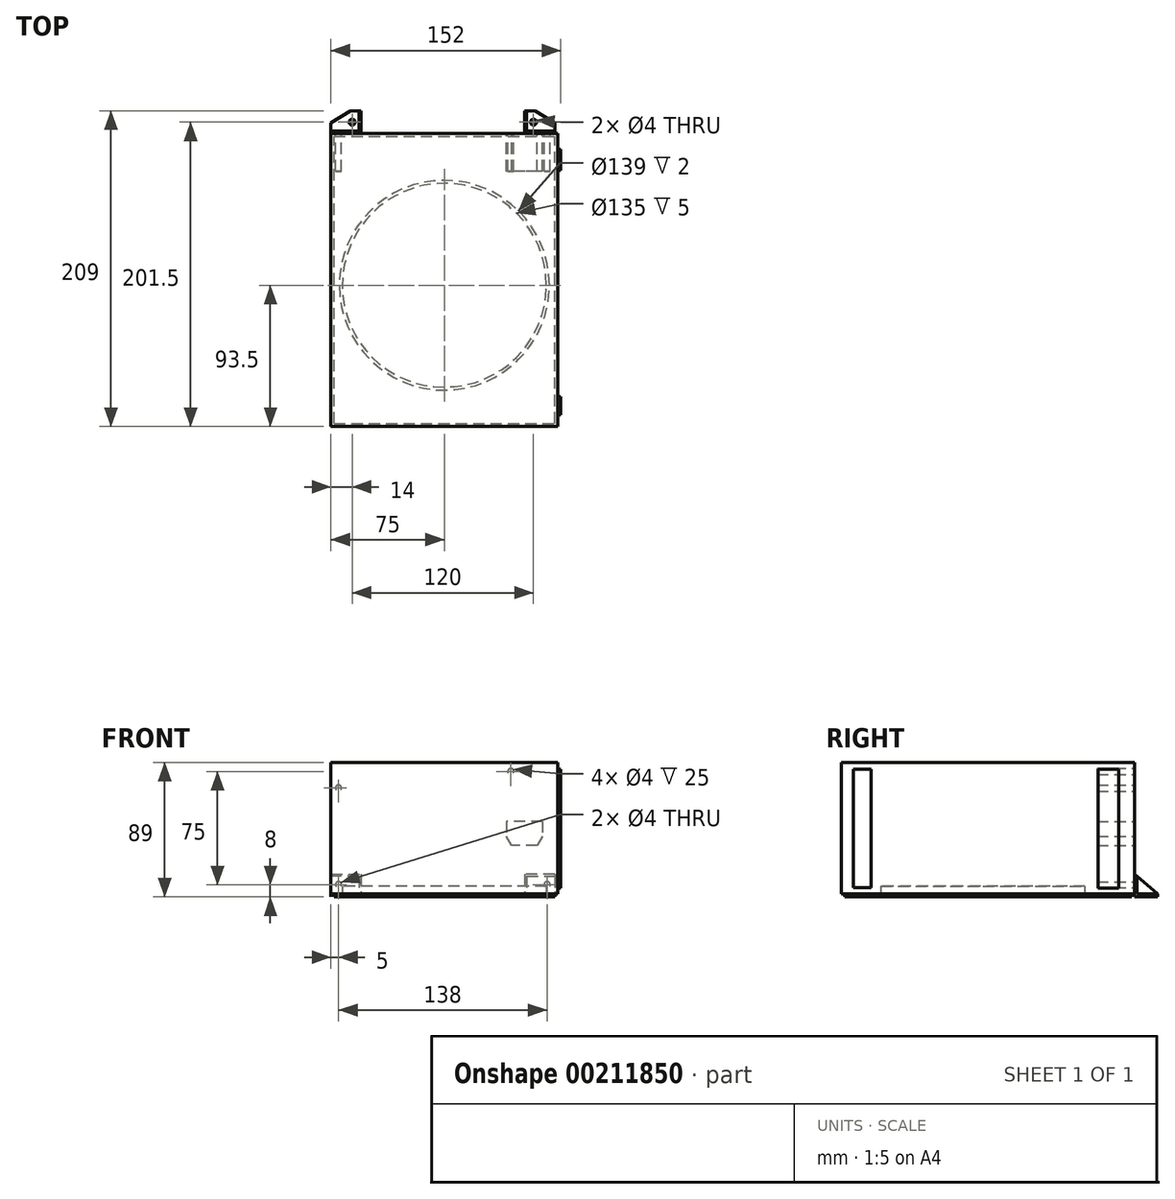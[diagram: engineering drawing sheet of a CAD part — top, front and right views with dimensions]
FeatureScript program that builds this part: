
annotation { "Feature Type Name" : "Feature", "Feature Type Description" : "" }
export const myFeature = defineFeature(function(context is Context, id is Id, definition is map)
    precondition{}
    {
        {
            var Q0;
            Q0=qCreatedBy(makeId("Top.planeOp"),FACE);
            var sketch = newSketch(context, id + "F0", { "sketchPlane" : qUnion([Q0])});
            skLineSegment(sketch, "E0.bottom", {"start": v(-75, 97) * mm, "end": v(75, 97) * mm});
            skLineSegment(sketch, "E0.top", {"start": v(-75, -97) * mm, "end": v(75, -97) * mm});
            skLineSegment(sketch, "E0.left", {"start": v(-75, 97) * mm, "end": v(-75, -97) * mm});
            skLineSegment(sketch, "E0.right", {"start": v(75, 97) * mm, "end": v(75, -97) * mm});
            skLineSegment(sketch, "E1", {"start": v(0, 0) * mm, "end": v(0, 97) * mm, "construction": true});
            skLineSegment(sketch, "E2", {"start": v(0, 0) * mm, "end": v(0, -97) * mm, "construction": true});
            skLineSegment(sketch, "E3", {"start": v(0, 0) * mm, "end": v(75, 0) * mm, "construction": true});
            skLineSegment(sketch, "E4", {"start": v(0, 0) * mm, "end": v(-75, 0) * mm, "construction": true});
            skCircle(sketch, "E5", {"center": v(0, -3.5) * mm, "radius": 67.5 * mm});
            skSolve(sketch);
        }
        {
            var Q0;
            Q0=makeQuery(id+"F0.imprint","IMPRINT",FACE,{"disambiguationData":[TD([[makeQuery(id+"F0.imprint","IMPRINT",EDGE,{"derivedFrom":sQuery(id+"F0.wireOp",EDGE,"E0.bottom")}),-1.0]])]});
            var Q1;
            Q1=makeQuery(id+"F0.imprint","IMPRINT",FACE,{"disambiguationData":[TD([[makeQuery(id+"F0.imprint","IMPRINT",EDGE,{"derivedFrom":sQuery(id+"F0.wireOp",EDGE,"E5")}),1.0]])]});
            extrude(context, id + "F1", {"entities" : qUnion([Q0, Q1]), "depth" : 87 * mm});
        }
        {
            var Q0;
            Q0=makeQuery(id+"F0.imprint","IMPRINT",FACE,{"disambiguationData":[TD([[makeQuery(id+"F0.imprint","IMPRINT",EDGE,{"derivedFrom":sQuery(id+"F0.wireOp",EDGE,"E5")}),1.0]])]});
            extrude(context, id + "F2", {"entities" : qUnion([Q0]), "operationType" : NewBodyOperationType.REMOVE, "depth" : 5 * mm});
        }
        {
            var Q0;
            Q0=makeQuery(id+"F1.opExtrude","SWEPT_FACE",FACE,{"disambiguationData":[OSD([sQuery(id+"F0.wireOp",EDGE,"E0.bottom")])]});
            var sketch = newSketch(context, id + "F3", { "sketchPlane" : qUnion([Q0])});
            skLineSegment(sketch, "E6.bottom", {"start": v(-65, 48) * mm, "end": v(-41, 48) * mm});
            skLineSegment(sketch, "E6.top", {"start": v(-61.5, 32) * mm, "end": v(-44.5, 32) * mm});
            skLineSegment(sketch, "E6.left", {"start": v(-65, 48) * mm, "end": v(-65, 38.06) * mm});
            skLineSegment(sketch, "E6.right", {"start": v(-41, 48) * mm, "end": v(-41, 38.06) * mm});
            skLineSegment(sketch, "E7", {"start": v(-65, 38.06) * mm, "end": v(-61.5, 32) * mm});
            skLineSegment(sketch, "E8", {"start": v(-44.5, 32) * mm, "end": v(-41, 38.06) * mm});
            skPoint(sketch, "E9.orphan", {"position": v(-65, 32) * mm});
            skPoint(sketch, "E10.orphan", {"position": v(-41, 32) * mm});
            skCircle(sketch, "E11", {"center": v(-44, 81) * mm, "radius": 2 * mm});
            skCircle(sketch, "E12", {"center": v(70, 70) * mm, "radius": 2 * mm});
            skCircle(sketch, "E13", {"center": v(70, 6) * mm, "radius": 2 * mm});
            skCircle(sketch, "E14", {"center": v(-68, 6) * mm, "radius": 2 * mm});
            skLineSegment(sketch, "E15", {"start": v(-91.51, 6) * mm, "end": v(111.2, 6) * mm, "construction": true});
            skLineSegment(sketch, "E16", {"start": v(70, 99.51) * mm, "end": v(70, -34.47) * mm, "construction": true});
            skSolve(sketch);
        }
        {
            var Q0;
            Q0 = qSketchRegion(id + "F3", true);
            extrude(context, id + "F4", {"entities" : qUnion([Q0]), "operationType" : NewBodyOperationType.REMOVE, "oppositeDirection" : true, "depth" : 25 * mm});
        }
        {
            var Q0;
            Q0=makeQuery(id+"F1.opExtrude","CAP_FACE",FACE,{"disambiguationData":[OSD([sQuery(id+"F0.wireOp",EDGE,"E0.bottom"),sQuery(id+"F0.wireOp",EDGE,"E0.top"),sQuery(id+"F0.wireOp",EDGE,"E0.left"),sQuery(id+"F0.wireOp",EDGE,"E0.right")])],"isStart":true});
            var sketch = newSketch(context, id + "F5", { "sketchPlane" : qUnion([Q0])});
            skLineSegment(sketch, "E17.bottom", {"start": v(-73, 95) * mm, "end": v(73, 95) * mm});
            skLineSegment(sketch, "E17.top", {"start": v(-73, -95) * mm, "end": v(73, -95) * mm});
            skLineSegment(sketch, "E17.left", {"start": v(-73, 95) * mm, "end": v(-73, -95) * mm});
            skLineSegment(sketch, "E17.right", {"start": v(73, 95) * mm, "end": v(73, -95) * mm});
            skLineSegment(sketch, "E18", {"start": v(0, 95) * mm, "end": v(0, 97) * mm, "construction": true});
            skLineSegment(sketch, "E19", {"start": v(73, 0) * mm, "end": v(75, 0) * mm, "construction": true});
            skLineSegment(sketch, "E20", {"start": v(0, -95) * mm, "end": v(0, -97) * mm, "construction": true});
            skLineSegment(sketch, "E21", {"start": v(-73, 0) * mm, "end": v(-75, 0) * mm, "construction": true});
            skCircle(sketch, "E22", {"center": v(0, 3.5) * mm, "radius": 69.5 * mm});
            skSolve(sketch);
        }
        {
            var Q0;
            Q0 = qSketchRegion(id + "F5", true);
            extrude(context, id + "F6", {"entities" : qUnion([Q0]), "depth" : 2 * mm});
        }
        {
            var Q0;
            Q0=makeQuery(id+"F1.opExtrude","CAP_FACE",FACE,{"disambiguationData":[OSD([sQuery(id+"F0.wireOp",EDGE,"E0.bottom"),sQuery(id+"F0.wireOp",EDGE,"E0.top"),sQuery(id+"F0.wireOp",EDGE,"E0.left"),sQuery(id+"F0.wireOp",EDGE,"E0.right")])],"isStart":true});
            cPlane(context, id + "F7", {"entities" : qUnion([Q0]), "cplaneType" : CPlaneType.OFFSET, "offset" : 2 * mm, "width" : 150 * mm, "height" : 150 * mm});
        }
        {
            var Q0;
            Q0=qCreatedBy(id+"F7.planeOp",FACE);
            var sketch = newSketch(context, id + "F8", { "sketchPlane" : qUnion([Q0])});
            skLineSegment(sketch, "E23", {"start": v(-75, -97) * mm, "end": v(-55, -97) * mm});
            skLineSegment(sketch, "E24", {"start": v(-55, -97) * mm, "end": v(-55, -112) * mm});
            skLineSegment(sketch, "E25", {"start": v(-55, -112) * mm, "end": v(-62, -112) * mm});
            skLineSegment(sketch, "E26", {"start": v(-62, -112) * mm, "end": v(-75, -104) * mm});
            skLineSegment(sketch, "E27", {"start": v(-75, -104) * mm, "end": v(-75, -97) * mm});
            skLineSegment(sketch, "E28.bottom", {"start": v(-75, -118.5) * mm, "end": v(-56.5, -118.5) * mm});
            skLineSegment(sketch, "E28.top", {"start": v(-75, -98.5) * mm, "end": v(-56.5, -98.5) * mm});
            skLineSegment(sketch, "E28.left", {"start": v(-75, -118.5) * mm, "end": v(-75, -98.5) * mm});
            skLineSegment(sketch, "E28.right", {"start": v(-56.5, -118.5) * mm, "end": v(-56.5, -98.5) * mm});
            skLineSegment(sketch, "E29", {"start": v(-56.5, -107.16) * mm, "end": v(-55, -107.16) * mm, "construction": true});
            skLineSegment(sketch, "E30", {"start": v(-65.75, -98.5) * mm, "end": v(-65.75, -97) * mm, "construction": true});
            skCircle(sketch, "E31", {"center": v(-61, -104.5) * mm, "radius": 2 * mm});
            skSolve(sketch);
        }
        {
            var Q0;
            Q0=makeQuery(id+"F8.imprint","IMPRINT",FACE,{"disambiguationData":[TD([[makeQuery(id+"F8.imprint","IMPRINT",EDGE,{"derivedFrom":sQuery(id+"F8.wireOp",EDGE,"E23")}),-1.0]])]});
            var Q1;
            {var subQ1=sQuery(id+"F8.wireOp",EDGE,"E28.top");Q1=makeQuery(id+"F8.imprint","IMPRINT",FACE,{"disambiguationData":[TD([[makeQuery(id+"F8.imprint","IMPRINT",EDGE,{"derivedFrom":subQ1}),-1.0]])]});}
            extrude(context, id + "F9", {"entities" : qUnion([Q0, Q1]), "oppositeDirection" : true, "depth" : 15 * mm});
        }
        {
            var Q0;
            Q0=qCreatedBy(id+"F7.planeOp",FACE);
            cPlane(context, id + "F10", {"entities" : qUnion([Q0]), "cplaneType" : CPlaneType.OFFSET, "offset" : 2 * mm, "oppositeDirection" : true, "width" : 150 * mm, "height" : 150 * mm});
        }
        {
            var Q0;
            {var subQ1=sQuery(id+"F8.wireOp",EDGE,"E28.top");Q0=makeQuery(id+"F8.imprint","IMPRINT",FACE,{"disambiguationData":[TD([[makeQuery(id+"F8.imprint","IMPRINT",EDGE,{"derivedFrom":subQ1}),-1.0]])]});}
            var Q1;
            Q1=qCreatedBy(id+"F10.planeOp",FACE);
            var Q2;
            Q2=qCreatedBy(id+"F10.planeOp",FACE);
            extrude(context, id + "F11", {"entities" : qUnion([Q0]), "operationType" : NewBodyOperationType.REMOVE, "endBound" : BoundingType.THROUGH_ALL, "oppositeDirection" : true, "endBoundEntityFace" : qUnion([Q1]), "depth" : 25 * mm, "hasSecondDirection" : true, "secondDirectionBound" : BoundingType.UP_TO_SURFACE, "secondDirectionOppositeDirection" : true, "secondDirectionBoundEntityFace" : qUnion([Q2]), "secondDirectionDepth" : 25 * mm});
        }
        {
            var Q0;
            Q0=makeQuery(id+"F9.opExtrude","SWEPT_FACE",FACE,{"disambiguationData":[OSD([sQuery(id+"F8.wireOp",EDGE,"E24")])]});
            var sketch = newSketch(context, id + "F12", { "sketchPlane" : qUnion([Q0])});
            skLineSegment(sketch, "E32", {"start": v(97, 13) * mm, "end": v(112, 0) * mm});
            skLineSegment(sketch, "E33", {"start": v(112, 0) * mm, "end": v(116.26, 0) * mm});
            skLineSegment(sketch, "E34", {"start": v(116.26, 0) * mm, "end": v(116.26, 17.16) * mm});
            skLineSegment(sketch, "E35", {"start": v(116.26, 17.16) * mm, "end": v(97, 17.16) * mm});
            skLineSegment(sketch, "E36", {"start": v(97, 17.16) * mm, "end": v(97, 13) * mm});
            skSolve(sketch);
        }
        {
            var Q0;
            Q0 = qSketchRegion(id + "F12", true);
            extrude(context, id + "F13", {"entities" : qUnion([Q0]), "operationType" : NewBodyOperationType.REMOVE, "oppositeDirection" : true, "depth" : 25 * mm});
        }
        {
            var Q0;
            Q0=makeQuery(id+"F11.boolean.opBoolean","COPY",FACE,{"derivedFrom":makeQuery(id+"F11.opExtrude","SWEPT_FACE",FACE,{"disambiguationData":[OSD([sQuery(id+"F8.wireOp",EDGE,"E28.top")])]})});
            var sketch = newSketch(context, id + "F14", { "sketchPlane" : qUnion([Q0])});
            skCircle(sketch, "E37", {"center": v(70, 6) * mm, "radius": 2 * mm});
            skSolve(sketch);
        }
        {
            var Q0;
            Q0 = qSketchRegion(id + "F14", true);
            extrude(context, id + "F15", {"entities" : qUnion([Q0]), "operationType" : NewBodyOperationType.REMOVE, "oppositeDirection" : true, "depth" : 3 * mm});
        }
        {
            var Q0;
            Q0=makeQuery(id+"F9.opExtrude","SWEPT_BODY",BODY,{"disambiguationData":[OSD([sQuery(id+"F8.wireOp",EDGE,"E23"),sQuery(id+"F8.wireOp",EDGE,"E24"),sQuery(id+"F8.wireOp",EDGE,"E25"),sQuery(id+"F8.wireOp",EDGE,"E26"),sQuery(id+"F8.wireOp",EDGE,"E27"),sQuery(id+"F8.wireOp",EDGE,"E28.left"),sQuery(id+"F8.wireOp",EDGE,"E31")])]});
            var Q1;
            Q1=qCreatedBy(makeId("Right.planeOp"),FACE);
            mirror(context, id + "F16", {"entities" : qUnion([Q0]), "mirrorPlane" : qUnion([Q1])});
        }
        {
            var Q0;
            Q0=makeQuery(id+"F16.opPattern","COPY",BODY,{"derivedFrom":makeQuery(id+"F9.opExtrude","SWEPT_BODY",BODY,{"disambiguationData":[OSD([sQuery(id+"F8.wireOp",EDGE,"E23"),sQuery(id+"F8.wireOp",EDGE,"E24"),sQuery(id+"F8.wireOp",EDGE,"E25"),sQuery(id+"F8.wireOp",EDGE,"E26"),sQuery(id+"F8.wireOp",EDGE,"E27"),sQuery(id+"F8.wireOp",EDGE,"E28.left"),sQuery(id+"F8.wireOp",EDGE,"E31")])]}),"instanceName":"1"});
            transform(context, id + "F17", {"entities" : qUnion([Q0]), "transformType" : TransformType.TRANSLATION_3D, "dx" : -2 * mm, "dy" : 0 * mm, "dz" : 0 * mm, "makeCopy" : false});
        }
        {
            var Q0;
            Q0=makeQuery(id+"F1.opExtrude","SWEPT_FACE",FACE,{"disambiguationData":[OSD([sQuery(id+"F0.wireOp",EDGE,"E0.right")])]});
            var sketch = newSketch(context, id + "F18", { "sketchPlane" : qUnion([Q0])});
            skLineSegment(sketch, "E38.bottom", {"start": v(-89.25, 82.4) * mm, "end": v(-77.36, 82.4) * mm});
            skLineSegment(sketch, "E38.top", {"start": v(-89.25, 4.09) * mm, "end": v(-77.36, 4.09) * mm});
            skLineSegment(sketch, "E38.left", {"start": v(-89.25, 82.4) * mm, "end": v(-89.25, 4.09) * mm});
            skLineSegment(sketch, "E38.right", {"start": v(-77.36, 82.4) * mm, "end": v(-77.36, 4.09) * mm});
            skLineSegment(sketch, "E39.bottom", {"start": v(72.72, 82.4) * mm, "end": v(86.47, 82.4) * mm});
            skLineSegment(sketch, "E39.top", {"start": v(72.72, 3.86) * mm, "end": v(86.47, 3.86) * mm});
            skLineSegment(sketch, "E39.left", {"start": v(72.72, 82.4) * mm, "end": v(72.72, 3.86) * mm});
            skLineSegment(sketch, "E39.right", {"start": v(86.47, 82.4) * mm, "end": v(86.47, 3.86) * mm});
            skSolve(sketch);
        }
        {
            var Q0;
            Q0 = qSketchRegion(id + "F18", true);
            extrude(context, id + "F19", {"entities" : qUnion([Q0]), "operationType" : NewBodyOperationType.ADD, "depth" : 2 * mm});
        }
    });
